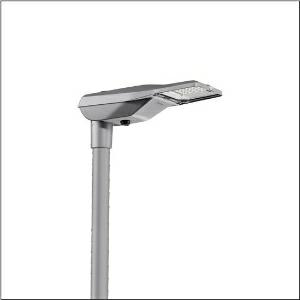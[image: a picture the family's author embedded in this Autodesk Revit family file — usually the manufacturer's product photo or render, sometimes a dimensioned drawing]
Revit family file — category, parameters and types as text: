
# Revit family: streetlight_sl_21_iq_micro___p0_8ab_5xe1r31u08cb_a822
name_source: partatom
category: Lighting Fixtures
units: mm (PartAtom-declared; Revit-internal decimal feet)

## family parameters
Cut with Voids When Loaded = No
Host = Face
Light Source = No
Part Type = Normal
Room Calculation Point = No
Round Connector Dimension = Use Diameter
Shared = No

## types (1)
- --- (1 x LED, 2570 lm, 19.1 W, 3000K)
    Apparent Load = 19 VA
    CIE Flux Codes = 36 71 98 100 100
    Color Rendering = 70
    Color Temperature = 3000K
    Default Elevation = 1800 mm
    Description = Streetlight SL 21 iQ micro, mast luminaire, primary light control with lens, of PMMA, primary optical cover: cover, of toughened safety glass, transparent, light distribution: P0.8aB, light emission: direct distribution, primary light characteristic: asymmetric, installation type: post-top, side-entry, LED, High Power LED, rated luminous flux: 2.570lm, luminous efficacy: 135lm/W, light colour: 730, colour temperature: 3000K, control gear: iQ-Street Remote, D4i with power reduction, control: pre-setting: logarithmic dimming characteristic, Street-Remote, Auto-Match, Temp-Guard, Lumen-Switch, Night-Set, Smart-Wire, Light-Fading, Desk-Remote (wireless, voltage-free reading and setting of iQ features in the workshop via application-optimized NFC function/RFID function), optimised constant luminous flux control (CLO 2.0), mains connection: 220..240V, AC, 50/60Hz, start of lifetime: 19W, end of service life: 20W, reduction: 9W, luminaire housing, of diecast aluminium, powder-coated, Siteco® metallic grey (DB 702S), corrosivity category C5 mid according to DIN EN ISO 12944, please order mast flange separately, inclination adjustable: 0°, 5°, 10°, 15°, sealing non-destructively replaceable, multi-level sealing system, length: 528mm, width: 235mm, height: 110mm, mast flange for spigot size: 42mm (side-entry): 5XC10008XM4, 60/48mm (side-entry/post-top): 5XC10108XM2, 76/60mm (side-entry/post-top): 5XC10108XM1, mounting height: 4..8m, Smart Interface below, protection rating (complete): IP66, insulation class (complete): insulation class II (safety insulation), certification: CE, ENEC, ENEC+, VDE, impact resistance: IK10, permissible operating ambient temperature for outdoor applications: -40..+50°C, standard-compliant lighting for roads and squares, packaging unit: 1 piece

Light Distribution: P0.8aB
    Height = 110 mm
    Lamp = 1 x LED
    Lamp Light Flux = 2570 lm
    Lamp Power = 19.1 W
    Lamp count = 1
    Length = 528 mm
    Luminous efficacy = 135 lm/W
    Manufacturer = Siteco
    ModVariant = No
    Model = 5XE1R31U08CB
    Number of Poles = 1
    OnlyDefault = Yes
    Power Factor = 1
    Product Name = Streetlight SL 21 iQ micro | P0.8aB
    Product group = mast luminaire | pylon top
    ProductGroupID = 6100
    Protection Class = Protection class II
    Protection Degree = IP 66
    RLX_Detail_Level = 1
    RLX_Emergency_Light_Flux = 0 lm
    RLX_Emergency_Type = 0
    RLX_Emergency_Type_DB = No
    RlxData = <blob elided: 99397 chars, md5=096e36a5>
    Socket = socket
    Standby Power = 0 W
    System Light Flux = 2570 lm
    System Power = 19 W
    Type Comments = factory setting: luminous flux: 100 % | dim-lin: 254 | 387 mA
    Type Image = l_1277290.jpg
    URL = http://relux.com
    VarID = @adj_097257
    Voltage = 0 V
    Weight = 0.00 kg
    Width = 235 mm

## geometry (parser evidence)
native form markers: Blend x4, Sweep x11
no freeform markers — native parametric forms only
